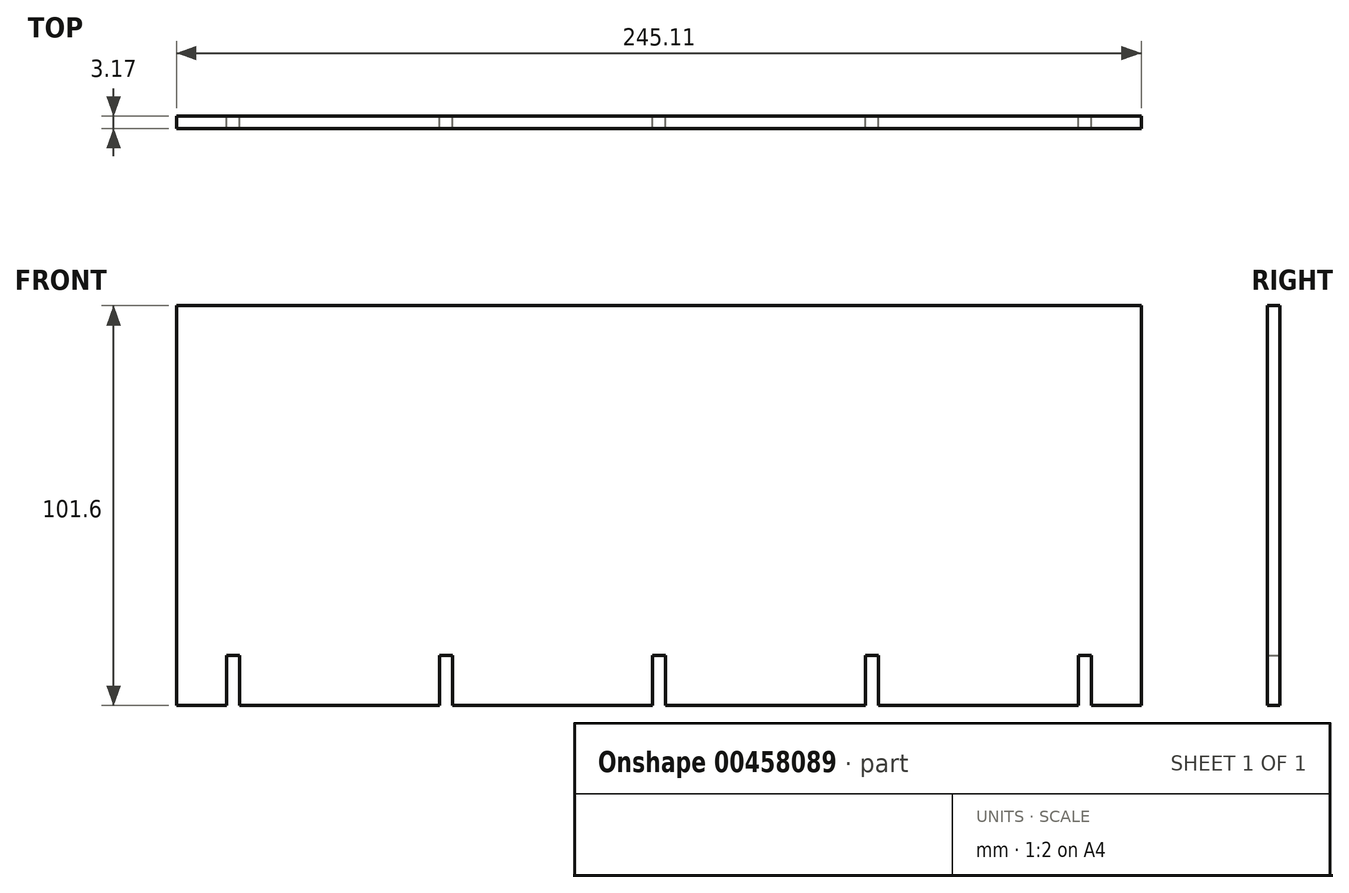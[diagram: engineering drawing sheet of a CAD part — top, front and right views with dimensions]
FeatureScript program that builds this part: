
annotation { "Feature Type Name" : "Feature", "Feature Type Description" : "" }
export const myFeature = defineFeature(function(context is Context, id is Id, definition is map)
    precondition{}
    {
        {
            var Q0;
            Q0=qCreatedBy(makeId("Front.planeOp"),FACE);
            var sketch = newSketch(context, id + "F0", { "sketchPlane" : qUnion([Q0])});
            skLineSegment(sketch, "E0", {"start": v(0, 0) * mm, "end": v(50.8, 0) * mm});
            skLineSegment(sketch, "E1", {"start": v(0, 12.7) * mm, "end": v(0, 0) * mm});
            skLineSegment(sketch, "E2", {"start": v(104.9, 12.7) * mm, "end": v(108.2, 12.7) * mm});
            skLineSegment(sketch, "E3", {"start": v(159, 12.7) * mm, "end": v(162.3, 12.7) * mm});
            skLineSegment(sketch, "E4", {"start": v(50.8, 12.7) * mm, "end": v(54.1, 12.7) * mm});
            skPoint(sketch, "E5.start.orphan", {"position": v(162.3, 0) * mm});
            skPoint(sketch, "E6.start.orphan", {"position": v(108.2, 0) * mm});
            skPoint(sketch, "E7.start.orphan", {"position": v(54.1, 0) * mm});
            skLineSegment(sketch, "E8", {"start": v(54.1, 12.7) * mm, "end": v(54.1, 0) * mm});
            skLineSegment(sketch, "E9", {"start": v(50.8, 12.7) * mm, "end": v(50.8, 0) * mm});
            skLineSegment(sketch, "E10", {"start": v(104.9, 12.7) * mm, "end": v(104.9, 0) * mm});
            skLineSegment(sketch, "E11", {"start": v(108.2, 12.7) * mm, "end": v(108.2, 0) * mm});
            skLineSegment(sketch, "E12", {"start": v(159, 12.7) * mm, "end": v(159, 0) * mm});
            skLineSegment(sketch, "E13", {"start": v(162.3, 12.7) * mm, "end": v(162.3, 0) * mm});
            skLineSegment(sketch, "E14.trimOffspring", {"start": v(54.1, 0) * mm, "end": v(104.9, 0) * mm});
            skLineSegment(sketch, "E15.trimOffspring", {"start": v(108.2, 0) * mm, "end": v(159, 0) * mm});
            skLineSegment(sketch, "E16.trimOffspring", {"start": v(162.3, 0) * mm, "end": v(213.1, 0) * mm});
            skLineSegment(sketch, "E17", {"start": v(-16, 101.6) * mm, "end": v(229.1, 101.6) * mm});
            skLineSegment(sketch, "E18.top", {"start": v(0, 12.7) * mm, "end": v(-3.3, 12.7) * mm});
            skLineSegment(sketch, "E19.top", {"start": v(213.1, 12.7) * mm, "end": v(216.4, 12.7) * mm});
            skLineSegment(sketch, "E20.top", {"start": v(216.4, 0) * mm, "end": v(229.1, 0) * mm});
            skLineSegment(sketch, "E20.left", {"start": v(216.4, 12.7) * mm, "end": v(216.4, 0) * mm});
            skLineSegment(sketch, "E21.top", {"start": v(-3.3, 0) * mm, "end": v(-16, 0) * mm});
            skLineSegment(sketch, "E21.left", {"start": v(-3.3, 12.7) * mm, "end": v(-3.3, 0) * mm});
            skLineSegment(sketch, "E21.right", {"start": v(-16, 101.6) * mm, "end": v(-16, 0) * mm});
            skLineSegment(sketch, "E22", {"start": v(213.1, 12.7) * mm, "end": v(213.1, 0) * mm});
            skLineSegment(sketch, "E23", {"start": v(229.1, 101.6) * mm, "end": v(229.1, 0) * mm});
            skSolve(sketch);
        }
        {
            var Q0;
            Q0=makeQuery(id+"F0.imprint","IMPRINT",FACE,{"disambiguationData":[TD([[makeQuery(id+"F0.imprint","IMPRINT",EDGE,{"derivedFrom":sQuery(id+"F0.wireOp",EDGE,"E0")}),1.0]])]});
            extrude(context, id + "F1", {"entities" : qUnion([Q0]), "depth" : 3.17 * mm, "offsetDistance" : 25.4 * mm});
        }
    });
